# Revit family: Shower-Shower_Door-KOHLER-Composed-K-27715.rfa_
name_source: partatom
category: Specialty Equipment
units: mm (PartAtom-declared; Revit-internal decimal feet)

## family parameters
Cut with Voids When Loaded = No
Host = Face
OmniClass Number = 23.31.17.17
OmniClass Title = Shower Enclosures
Part Type = Normal
Room Calculation Point = No
Round Connector Dimension = Use Diameter
Shared = No

## types (3) — shared parameters
ADA Compliant = No
Assembly Code = C1030200
Date Modified = 06/29/2023
Default Elevation = 4"
Description = 3/8 Inch Pivot Glass And Hardware,No Handle
Height = 71 3/4"
Length = 5 1/2"
Manufacturer = Kohler Co.
Master Format 2014 = 10 28 19.16
Master Format 2014 Name = Shower Doors
Material = Premium Metal Construction
Product Documentation Link = https://www.us.kohler.com
Product Name = Composed
Product Page URL = http://www.us.kohler.com
URL = https://www.us.kohler.com
WaterSense Certified = No
Width = 46 15/16"

## per-type parameters (varying)
| type | Finish | Model | Secondary Finish | Type |
| SHP-Bright Polished Silver | Kohler-Metal-SHP-Bright_Polished_Silver | K-27715-10L-SHP | Kohler-Metal-CP-Polished_Chrome | 1 |
| BNK-Anodized Brushed Nickel | Kohler-Metal-BNK-Anodized_Brushed_Nickel | K-27715-10L-BNK | Kohler-Metal-BN-Vibrant_Brushed_Nickel | 2 |
| BL-Matte Black | Kohler-Metal-BL-Matte_Black | K-27715-10L-BL | Kohler-Metal-BL-Matte_Black | 3 |

## geometry (parser evidence)
native form markers: Sweep x4
no freeform markers — native parametric forms only
